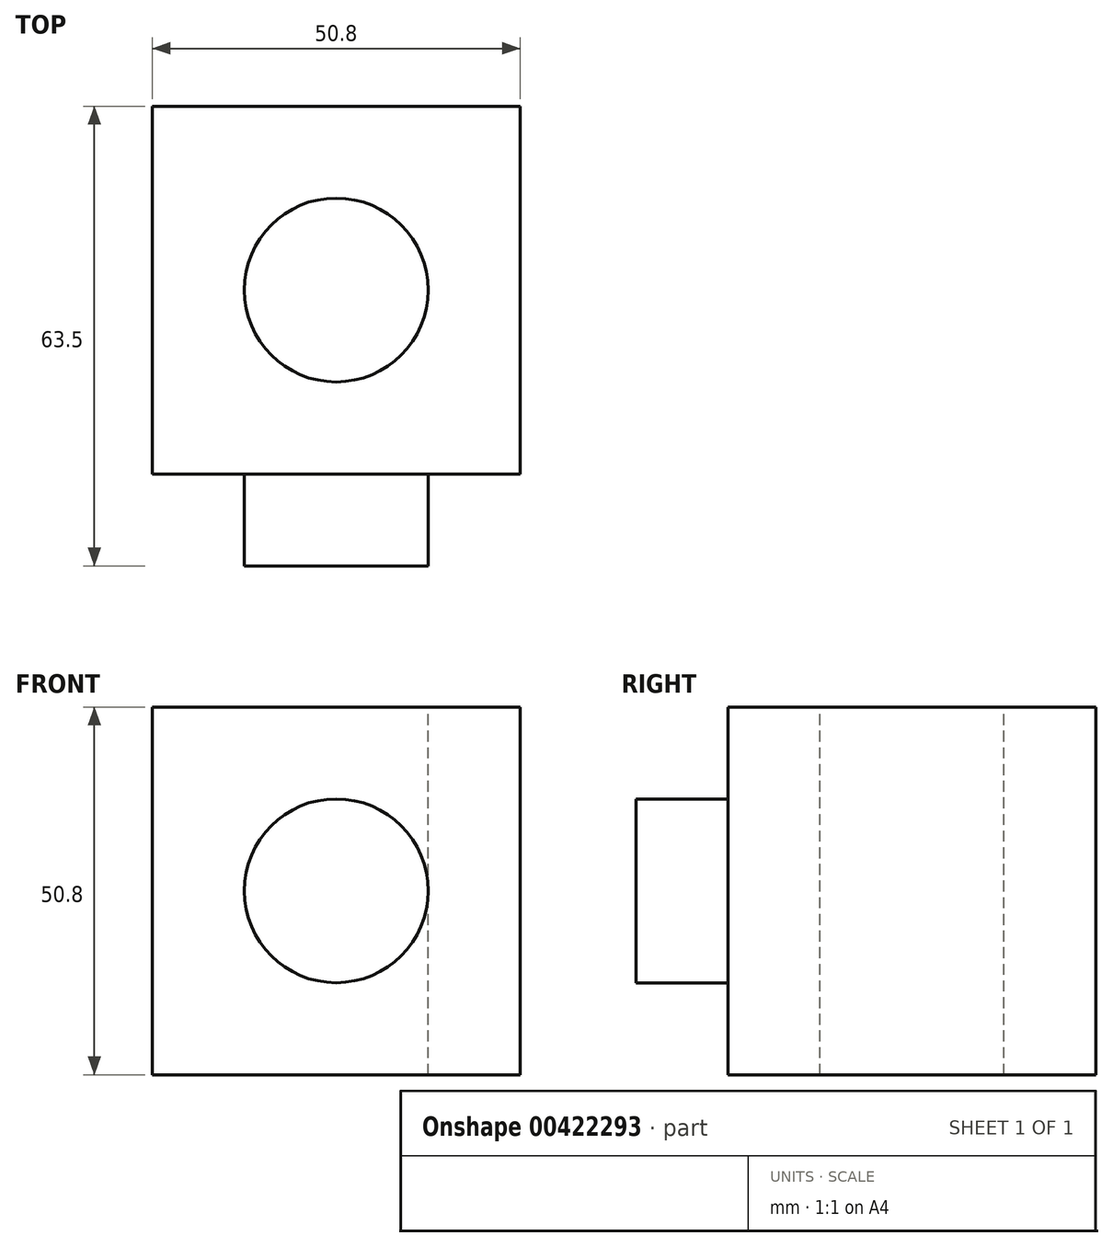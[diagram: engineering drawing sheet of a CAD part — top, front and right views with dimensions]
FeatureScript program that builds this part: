
annotation { "Feature Type Name" : "Feature", "Feature Type Description" : "" }
export const myFeature = defineFeature(function(context is Context, id is Id, definition is map)
    precondition{}
    {
        {
            var Q0;
            Q0=qCreatedBy(makeId("Front.planeOp"),FACE);
            var sketch = newSketch(context, id + "F0", { "sketchPlane" : qUnion([Q0])});
            skLineSegment(sketch, "E0.bottom", {"start": v(-31.96, 29.2) * mm, "end": v(18.84, 29.2) * mm});
            skLineSegment(sketch, "E0.top", {"start": v(-31.96, -21.6) * mm, "end": v(18.84, -21.6) * mm});
            skLineSegment(sketch, "E0.left", {"start": v(-31.96, 29.2) * mm, "end": v(-31.96, -21.6) * mm});
            skLineSegment(sketch, "E0.right", {"start": v(18.84, 29.2) * mm, "end": v(18.84, -21.6) * mm});
            skSolve(sketch);
        }
        {
            var Q0;
            Q0 = qSketchRegion(id + "F0", true);
            extrude(context, id + "F1", {"entities" : qUnion([Q0]), "depth" : 50.8 * mm});
        }
        {
            var Q0;
            Q0=makeQuery(id+"F1.opExtrude","CAP_FACE",FACE,{"disambiguationData":[OSD([sQuery(id+"F0.wireOp",EDGE,"E0.bottom"),sQuery(id+"F0.wireOp",EDGE,"E0.top"),sQuery(id+"F0.wireOp",EDGE,"E0.left"),sQuery(id+"F0.wireOp",EDGE,"E0.right")])],"isStart":false});
            var sketch = newSketch(context, id + "F2", { "sketchPlane" : qUnion([Q0])});
            skCircle(sketch, "E1", {"center": v(-6.56, 3.8) * mm, "radius": 12.7 * mm});
            skSolve(sketch);
        }
        {
            var Q0;
            Q0=makeQuery(id+"F2.imprint","IMPRINT",FACE,{"disambiguationData":[TD([[makeQuery(id+"F2.imprint","IMPRINT",EDGE,{"derivedFrom":sQuery(id+"F2.wireOp",EDGE,"E1")}),1.0]])]});
            extrude(context, id + "F3", {"entities" : qUnion([Q0]), "operationType" : NewBodyOperationType.ADD, "depth" : 12.7 * mm});
        }
        {
            var Q0;
            Q0=makeQuery(id+"F1.opExtrude","SWEPT_FACE",FACE,{"disambiguationData":[OSD([sQuery(id+"F0.wireOp",EDGE,"E0.bottom")])]});
            var sketch = newSketch(context, id + "F4", { "sketchPlane" : qUnion([Q0])});
            skCircle(sketch, "E2", {"center": v(-6.56, -25.4) * mm, "radius": 12.7 * mm});
            skSolve(sketch);
        }
        {
            var Q0;
            Q0=makeQuery(id+"F4.imprint","IMPRINT",FACE,{"disambiguationData":[TD([[makeQuery(id+"F4.imprint","IMPRINT",EDGE,{"derivedFrom":sQuery(id+"F4.wireOp",EDGE,"E2")}),1.0]])]});
            extrude(context, id + "F5", {"entities" : qUnion([Q0]), "operationType" : NewBodyOperationType.REMOVE, "oppositeDirection" : true, "depth" : 50.8 * mm});
        }
    });
